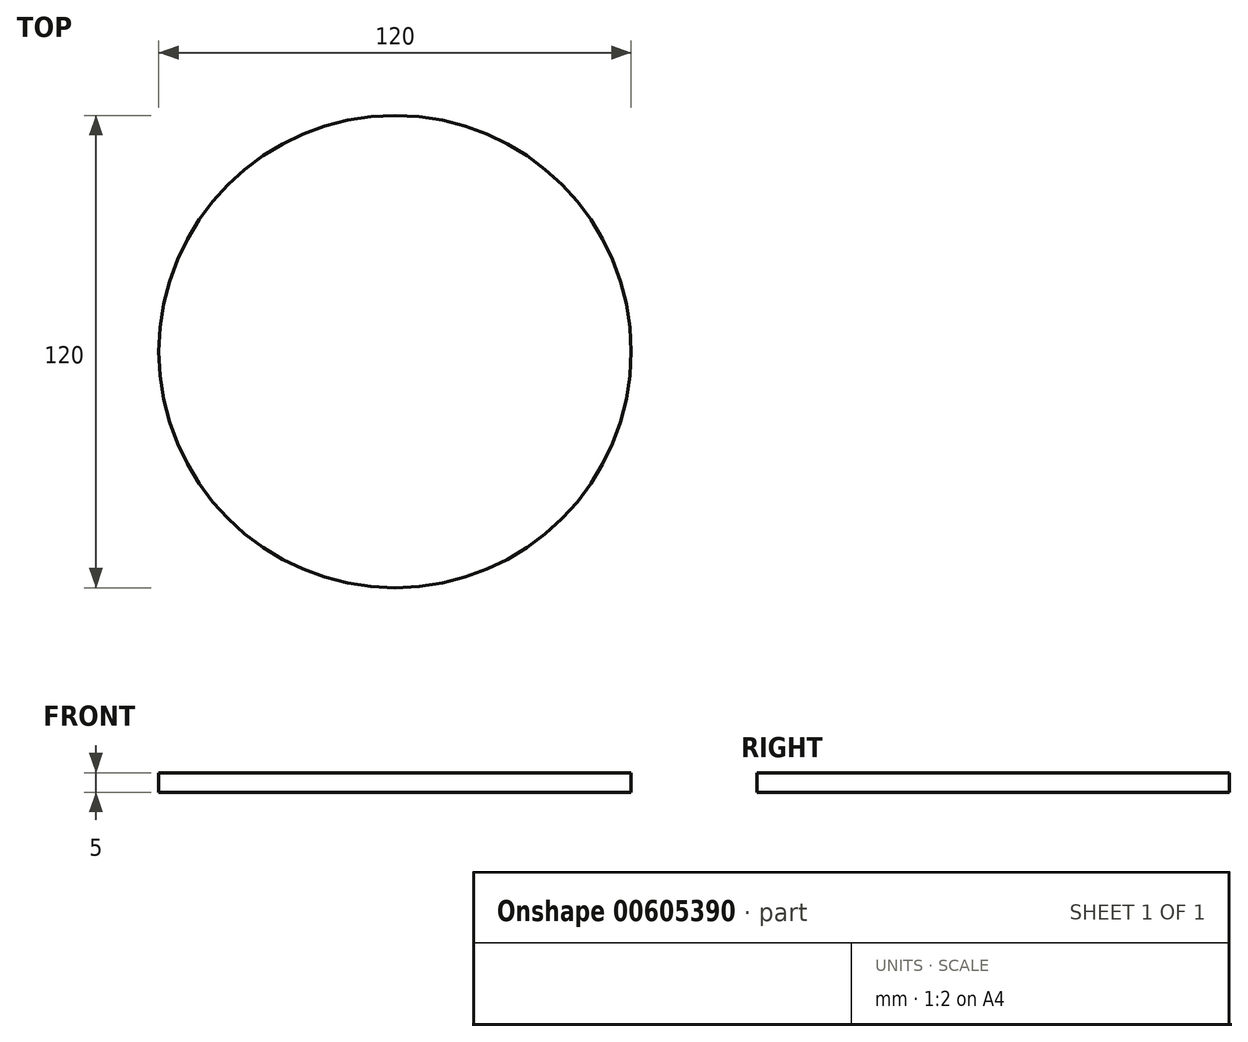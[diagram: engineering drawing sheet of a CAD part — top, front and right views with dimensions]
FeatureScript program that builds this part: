
annotation { "Feature Type Name" : "Feature", "Feature Type Description" : "" }
export const myFeature = defineFeature(function(context is Context, id is Id, definition is map)
    precondition{}
    {
        {
            var Q0;
            Q0=qCreatedBy(makeId("Top.planeOp"),FACE);
            var sketch = newSketch(context, id + "F0", { "sketchPlane" : qUnion([Q0])});
            skCircle(sketch, "E0", {"center": v(0, 0) * mm, "radius": 60 * mm});
            skSolve(sketch);
        }
        {
            var Q0;
            Q0=makeQuery(id+"F0.imprint","IMPRINT",FACE,{"disambiguationData":[TD([[makeQuery(id+"F0.imprint","IMPRINT",EDGE,{"derivedFrom":sQuery(id+"F0.wireOp",EDGE,"E0")}),1.0]])]});
            extrude(context, id + "F1", {"entities" : qUnion([Q0]), "depth" : 5 * mm, "offsetDistance" : 25 * mm});
        }
    });
